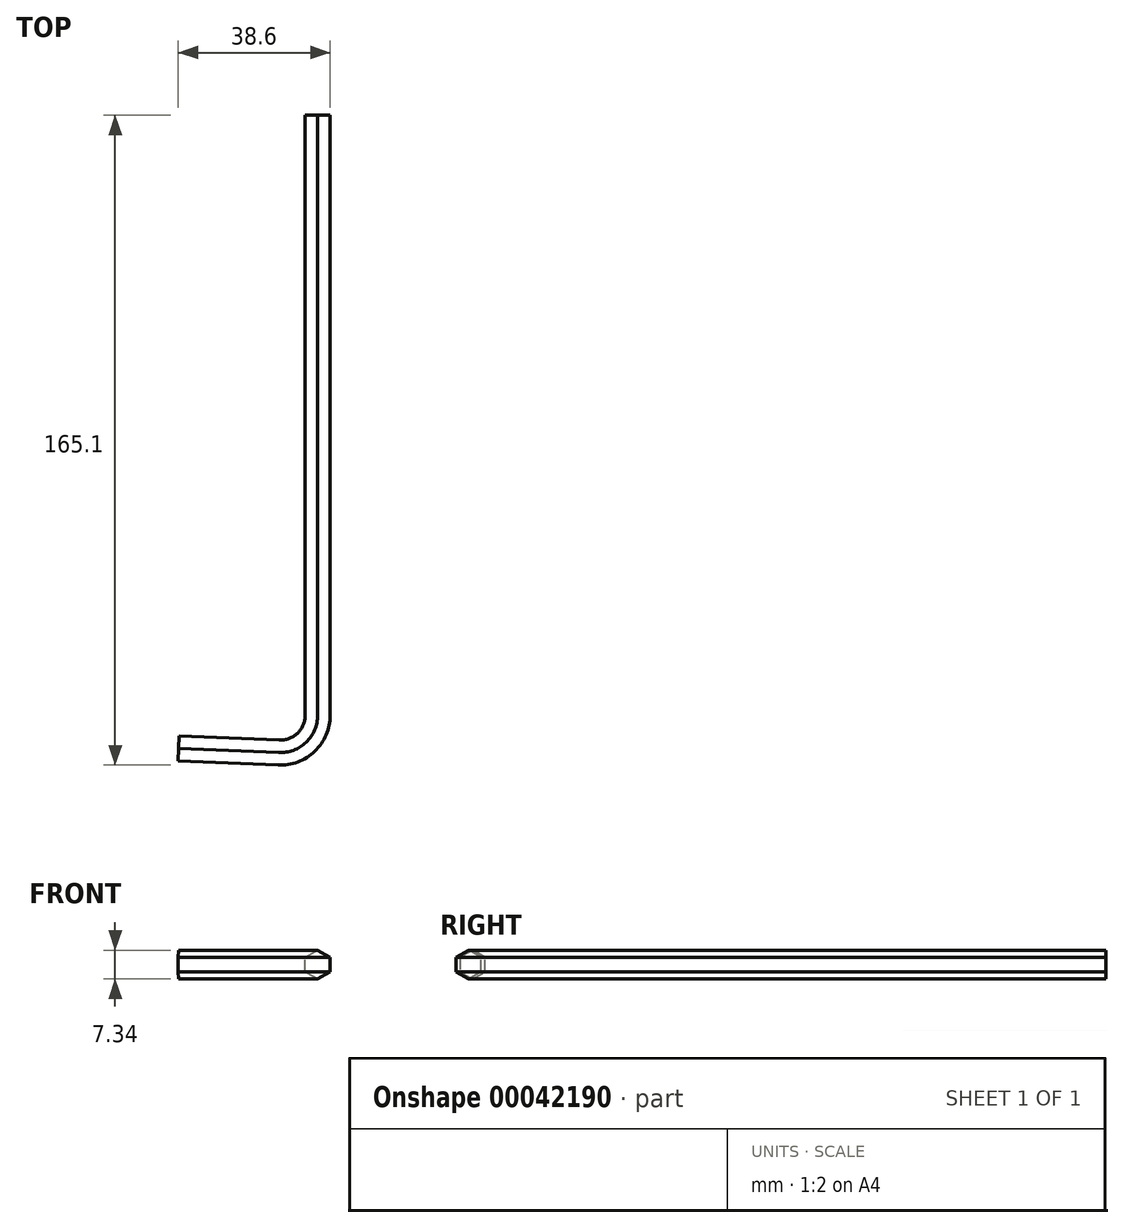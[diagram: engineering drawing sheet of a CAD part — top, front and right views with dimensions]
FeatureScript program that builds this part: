
annotation { "Feature Type Name" : "Feature", "Feature Type Description" : "" }
export const myFeature = defineFeature(function(context is Context, id is Id, definition is map)
    precondition{}
    {
        {
            var Q0;
            Q0=qCreatedBy(makeId("Front.planeOp"),FACE);
            var sketch = newSketch(context, id + "F0", { "sketchPlane" : qUnion([Q0])});
            skLineSegment(sketch, "E0", {"start": v(0, 0) * mm, "end": v(0, 3.85) * mm, "construction": true});
            skLineSegment(sketch, "E1", {"start": v(-2.96, 0) * mm, "end": v(3.17, 0) * mm, "construction": true});
            skCircle(sketch, "E2.cCircle", {"center": v(0, 0) * mm, "radius": 3.18 * mm, "construction": true});
            skLineSegment(sketch, "E2.0", {"start": v(3.18, 1.83) * mm, "end": v(3.18, -1.83) * mm});
            skLineSegment(sketch, "E2.1", {"start": v(3.17, -1.83) * mm, "end": v(0, -3.67) * mm});
            skLineSegment(sketch, "E2.2", {"start": v(0, -3.67) * mm, "end": v(-3.17, -1.83) * mm});
            skLineSegment(sketch, "E2.3", {"start": v(-3.17, -1.83) * mm, "end": v(-3.18, 1.83) * mm});
            skLineSegment(sketch, "E2.4", {"start": v(-3.18, 1.83) * mm, "end": v(0, 3.67) * mm});
            skLineSegment(sketch, "E2.5", {"start": v(0, 3.67) * mm, "end": v(3.17, 1.83) * mm});
            skPoint(sketch, "E2.0.midPoint", {"position": v(3.18, 0) * mm});
            skSolve(sketch);
        }
        {
            var Q0;
            Q0=makeQuery(id+"F0.imprint","IMPRINT",FACE,{"disambiguationData":[TD([[makeQuery(id+"F0.imprint","IMPRINT",EDGE,{"derivedFrom":sQuery(id+"F0.wireOp",EDGE,"E2.0")}),-1.0]])]});
            extrude(context, id + "F1", {"entities" : qUnion([Q0]), "depth" : 152.4 * mm});
        }
        {
            var Q0;
            Q0=makeQuery(id+"F1.opExtrude","CAP_FACE",FACE,{"disambiguationData":[OSD([sQuery(id+"F0.wireOp",EDGE,"E2.0"),sQuery(id+"F0.wireOp",EDGE,"E2.1"),sQuery(id+"F0.wireOp",EDGE,"E2.2"),sQuery(id+"F0.wireOp",EDGE,"E2.3"),sQuery(id+"F0.wireOp",EDGE,"E2.4"),sQuery(id+"F0.wireOp",EDGE,"E2.5")])],"isStart":false});
            var sketch = newSketch(context, id + "F2", { "sketchPlane" : qUnion([Q0])});
            skLineSegment(sketch, "E3.0", {"start": v(-3.17, -1.83) * mm, "end": v(-3.18, 1.83) * mm});
            skLineSegment(sketch, "E4", {"start": v(-9.53, 0) * mm, "end": v(-9.53, 1.83) * mm, "construction": true});
            skPoint(sketch, "E4.startSnap0", {"position": v(-3.18, 0) * mm});
            skSolve(sketch);
        }
        {
            var Q0;
            Q0 = qSketchRegion(id + "F2", true);
            var Q1;
            Q1=makeQuery(id+"F2.imprint","IMPRINT",FACE,{"disambiguationData":[TD([[makeQuery(id+"F2.imprint","IMPRINT",EDGE,{"derivedFrom":sQuery(id+"F2.wireOp",EDGE,"E3.0")}),-1.0]])]});
            var Q2;
            Q2=sQuery(id+"F2.wireOp",EDGE,"E4");
            revolve(context, id + "F3", {"operationType" : NewBodyOperationType.ADD, "entities" : qUnion([Q0, Q1]), "axis" : qUnion([Q2]), "revolveType" : RevolveType.ONE_DIRECTION, "oppositeDirection" : true, "angle" : 92.31 * degree});
        }
        {
            var Q0;
            Q0=makeQuery(id+"F3.opRevolve","CAP_FACE",FACE,{"disambiguationData":[OSD([sQuery(id+"F0.wireOp",EDGE,"E2.0"),sQuery(id+"F0.wireOp",EDGE,"E2.1"),sQuery(id+"F0.wireOp",EDGE,"E2.2"),sQuery(id+"F0.wireOp",EDGE,"E2.4"),sQuery(id+"F0.wireOp",EDGE,"E2.5"),sQuery(id+"F2.wireOp",EDGE,"E3.0")])],"isStart":false});
            extrude(context, id + "F4", {"entities" : qUnion([Q0]), "operationType" : NewBodyOperationType.ADD, "depth" : 25.4 * mm});
        }
    });
